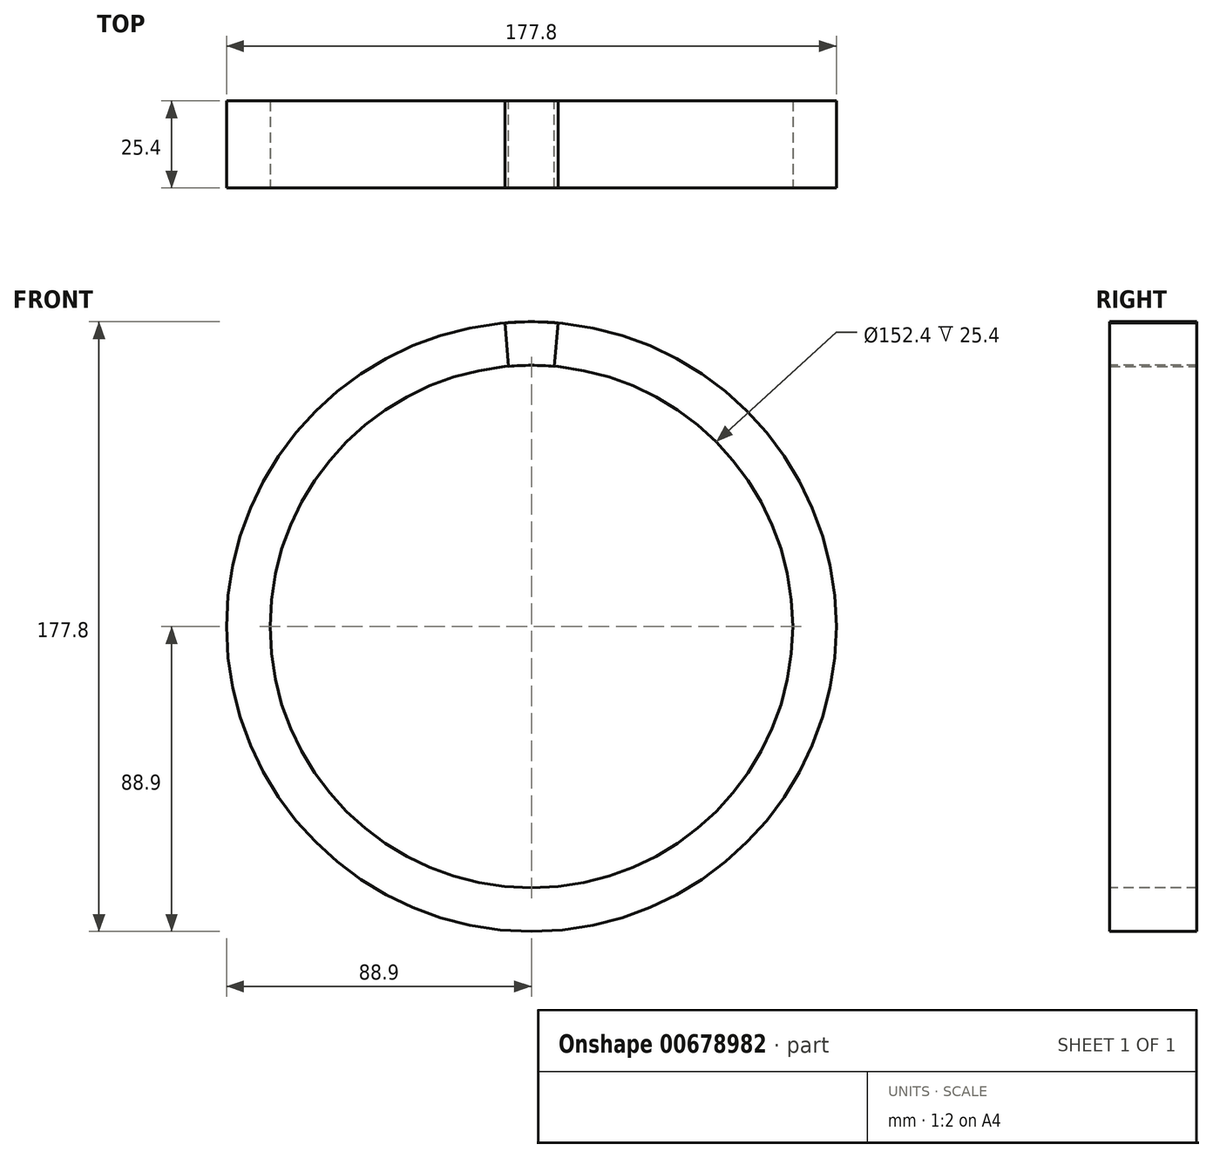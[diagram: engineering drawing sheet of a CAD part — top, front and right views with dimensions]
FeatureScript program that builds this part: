
annotation { "Feature Type Name" : "Feature", "Feature Type Description" : "" }
export const myFeature = defineFeature(function(context is Context, id is Id, definition is map)
    precondition{}
    {
        {
            var Q0;
            Q0=qCreatedBy(makeId("Right.planeOp"),FACE);
            var sketch = newSketch(context, id + "F0", { "sketchPlane" : qUnion([Q0])});
            skLineSegment(sketch, "E0.bottom", {"start": v(-12.75, 88.9) * mm, "end": v(12.65, 88.9) * mm});
            skLineSegment(sketch, "E0.top", {"start": v(-12.75, 76.2) * mm, "end": v(12.65, 76.2) * mm});
            skLineSegment(sketch, "E0.left", {"start": v(-12.75, 88.9) * mm, "end": v(-12.75, 76.2) * mm});
            skLineSegment(sketch, "E0.right", {"start": v(12.65, 88.9) * mm, "end": v(12.65, 76.2) * mm});
            skSolve(sketch);
        }
        {
            var Q0;
            Q0=qCreatedBy(makeId("Top.planeOp"),FACE);
            var sketch = newSketch(context, id + "F1", { "sketchPlane" : qUnion([Q0])});
            skLineSegment(sketch, "E1", {"start": v(0, 0) * mm, "end": v(0, 25.4) * mm});
            skCircle(sketch, "E2", {"center": v(0, 0) * mm, "radius": 12.7 * mm, "construction": true});
            skSolve(sketch);
        }
        {
            var Q0;
            Q0=makeQuery(id+"F0.imprint","IMPRINT",FACE,{"disambiguationData":[TD([[makeQuery(id+"F0.imprint","IMPRINT",EDGE,{"derivedFrom":sQuery(id+"F0.wireOp",EDGE,"E0.bottom")}),-1.0]])]});
            var Q1;
            Q1=sQuery(id+"F1.wireOp",EDGE,"E1");
            revolve(context, id + "F2", {"entities" : qUnion([Q0]), "axis" : qUnion([Q1]), "revolveType" : RevolveType.SYMMETRIC, "angle" : 10 * degree});
        }
        {
            var Q0;
            Q0=makeQuery(id+"F0.imprint","IMPRINT",FACE,{"disambiguationData":[TD([[makeQuery(id+"F0.imprint","IMPRINT",EDGE,{"derivedFrom":sQuery(id+"F0.wireOp",EDGE,"E0.bottom")}),-1.0]])]});
            var Q1;
            Q1=sQuery(id+"F1.wireOp",EDGE,"E1");
            revolve(context, id + "F3", {"entities" : qUnion([Q0]), "axis" : qUnion([Q1]), "revolveType" : RevolveType.FULL});
        }
        {
            var Q0;
            Q0=makeQuery(id+"F2.opRevolve","SWEPT_BODY",BODY,{"disambiguationData":[OSD([sQuery(id+"F0.wireOp",EDGE,"E0.bottom"),sQuery(id+"F0.wireOp",EDGE,"E0.top"),sQuery(id+"F0.wireOp",EDGE,"E0.left"),sQuery(id+"F0.wireOp",EDGE,"E0.right")])]});
            var Q1;
            Q1=makeQuery(id+"F3.opRevolve","SWEPT_BODY",BODY,{"disambiguationData":[OSD([sQuery(id+"F0.wireOp",EDGE,"E0.bottom"),sQuery(id+"F0.wireOp",EDGE,"E0.top"),sQuery(id+"F0.wireOp",EDGE,"E0.left"),sQuery(id+"F0.wireOp",EDGE,"E0.right")])]});
            transform(context, id + "F4", {"entities" : qUnion([Q0, Q1]), "transformType" : TransformType.TRANSLATION_3D, "dx" : 0 * mm, "dy" : 12.7 * mm, "dz" : 0 * mm, "makeCopy" : false});
        }
    });
